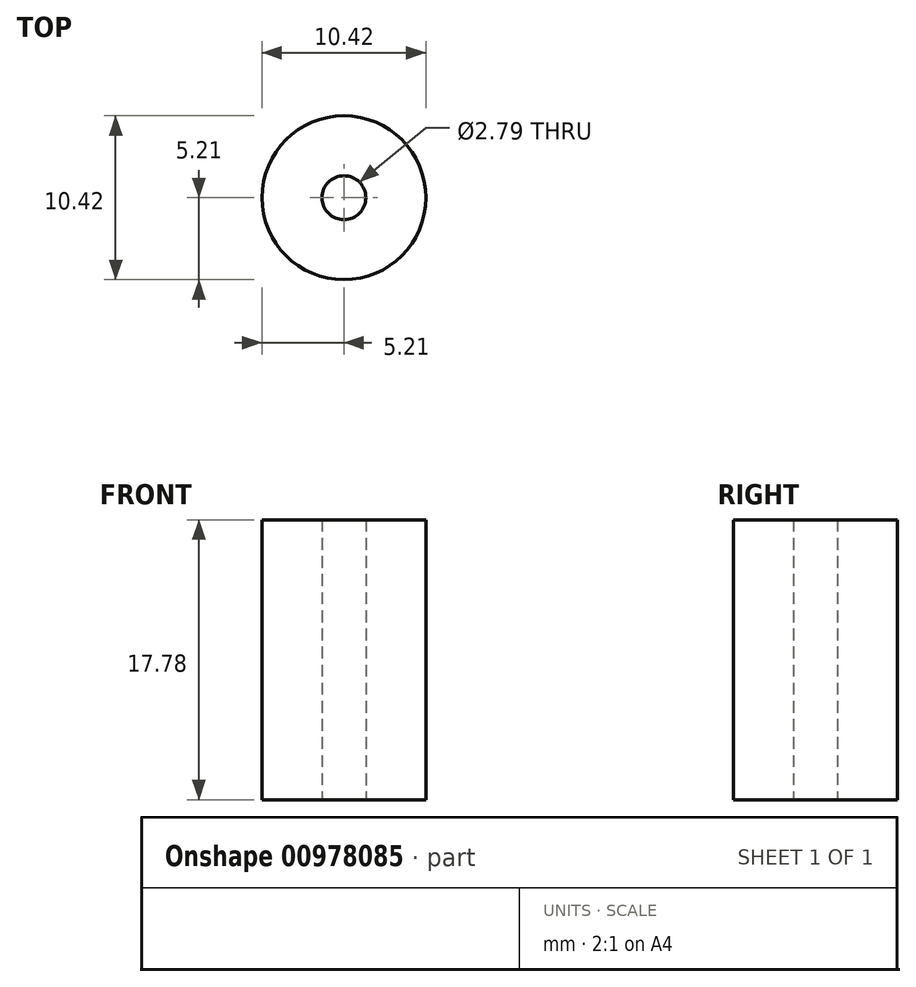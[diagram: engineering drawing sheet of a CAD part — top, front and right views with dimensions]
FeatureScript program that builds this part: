
annotation { "Feature Type Name" : "Feature", "Feature Type Description" : "" }
export const myFeature = defineFeature(function(context is Context, id is Id, definition is map)
    precondition{}
    {
        {
            var Q0;
            Q0=qCreatedBy(makeId("Top.planeOp"),FACE);
            var sketch = newSketch(context, id + "F0", { "sketchPlane" : qUnion([Q0])});
            skCircle(sketch, "E0", {"center": v(0, 0) * mm, "radius": 1.4 * mm});
            skCircle(sketch, "E1.0", {"center": v(0, 0) * mm, "radius": 5.2 * mm});
            skSolve(sketch);
        }
        {
            var Q0;
            Q0 = qSketchRegion(id + "F0", true);
            extrude(context, id + "F1", {"entities" : qUnion([Q0]), "depth" : 17.78 * mm, "offsetDistance" : 25.4 * mm});
        }
    });
